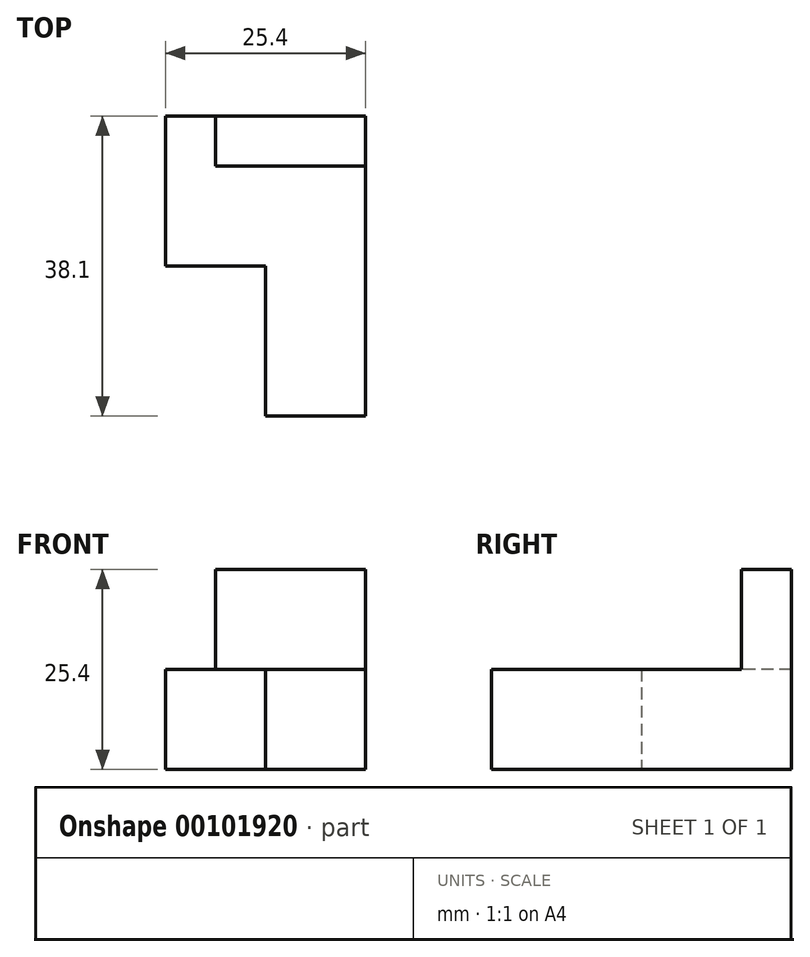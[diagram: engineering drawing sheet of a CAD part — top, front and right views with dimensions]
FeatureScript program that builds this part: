
annotation { "Feature Type Name" : "Feature", "Feature Type Description" : "" }
export const myFeature = defineFeature(function(context is Context, id is Id, definition is map)
    precondition{}
    {
        {
            var Q0;
            Q0=qCreatedBy(makeId("Front.planeOp"),FACE);
            var sketch = newSketch(context, id + "F0", { "sketchPlane" : qUnion([Q0])});
            skLineSegment(sketch, "E0.bottom", {"start": v(0, 0) * mm, "end": v(25.4, 0) * mm});
            skLineSegment(sketch, "E0.top", {"start": v(0, 25.4) * mm, "end": v(25.4, 25.4) * mm});
            skLineSegment(sketch, "E0.left", {"start": v(0, 0) * mm, "end": v(0, 25.4) * mm});
            skLineSegment(sketch, "E0.right", {"start": v(25.4, 0) * mm, "end": v(25.4, 25.4) * mm});
            skSolve(sketch);
        }
        {
            var Q0;
            Q0 = qSketchRegion(id + "F0", true);
            extrude(context, id + "F1", {"entities" : qUnion([Q0]), "endBound" : BoundingType.SYMMETRIC, "depth" : 38.1 * mm});
        }
        {
            var Q0;
            Q0=qCreatedBy(makeId("Top.planeOp"),FACE);
            var sketch = newSketch(context, id + "F2", { "sketchPlane" : qUnion([Q0])});
            skLineSegment(sketch, "E1", {"start": v(0, 0) * mm, "end": v(12.7, 0) * mm});
            skLineSegment(sketch, "E2", {"start": v(12.7, 0) * mm, "end": v(12.7, -19.05) * mm});
            skLineSegment(sketch, "E3", {"start": v(12.7, -19.05) * mm, "end": v(0, -19.05) * mm});
            skLineSegment(sketch, "E4", {"start": v(0, -19.05) * mm, "end": v(0, 0) * mm});
            skSolve(sketch);
        }
        {
            var Q0;
            Q0 = qSketchRegion(id + "F2", true);
            extrude(context, id + "F3", {"entities" : qUnion([Q0]), "operationType" : NewBodyOperationType.REMOVE, "endBound" : BoundingType.SYMMETRIC, "depth" : 107.3 * mm});
        }
        {
            var Q0;
            Q0=qCreatedBy(makeId("Right.planeOp"),FACE);
            var sketch = newSketch(context, id + "F4", { "sketchPlane" : qUnion([Q0])});
            skLineSegment(sketch, "E5.bottom", {"start": v(-19.05, 12.7) * mm, "end": v(12.7, 12.7) * mm});
            skLineSegment(sketch, "E5.top", {"start": v(-19.05, 25.4) * mm, "end": v(12.7, 25.4) * mm});
            skLineSegment(sketch, "E5.left", {"start": v(-19.05, 12.7) * mm, "end": v(-19.05, 25.4) * mm});
            skLineSegment(sketch, "E5.right", {"start": v(12.7, 12.7) * mm, "end": v(12.7, 25.4) * mm});
            skSolve(sketch);
        }
        {
            var Q0;
            Q0 = qSketchRegion(id + "F4", true);
            extrude(context, id + "F5", {"entities" : qUnion([Q0]), "operationType" : NewBodyOperationType.REMOVE, "depth" : 44.73 * mm});
        }
        {
            var Q0;
            Q0=qCreatedBy(makeId("Front.planeOp"),FACE);
            var sketch = newSketch(context, id + "F6", { "sketchPlane" : qUnion([Q0])});
            skLineSegment(sketch, "E6.bottom", {"start": v(0, 25.4) * mm, "end": v(6.35, 25.4) * mm});
            skLineSegment(sketch, "E6.top", {"start": v(0, 12.7) * mm, "end": v(6.35, 12.7) * mm});
            skLineSegment(sketch, "E6.left", {"start": v(0, 25.4) * mm, "end": v(0, 12.7) * mm});
            skLineSegment(sketch, "E6.right", {"start": v(6.35, 25.4) * mm, "end": v(6.35, 12.7) * mm});
            skSolve(sketch);
        }
        {
            var Q0;
            Q0=makeQuery(id+"F6.imprint","IMPRINT",FACE,{"disambiguationData":[TD([[makeQuery(id+"F6.imprint","IMPRINT",EDGE,{"derivedFrom":sQuery(id+"F6.wireOp",EDGE,"E6.bottom")}),-1.0]])]});
            extrude(context, id + "F7", {"entities" : qUnion([Q0]), "operationType" : NewBodyOperationType.REMOVE, "endBound" : BoundingType.THROUGH_ALL, "oppositeDirection" : true, "depth" : 25.4 * mm});
        }
    });
